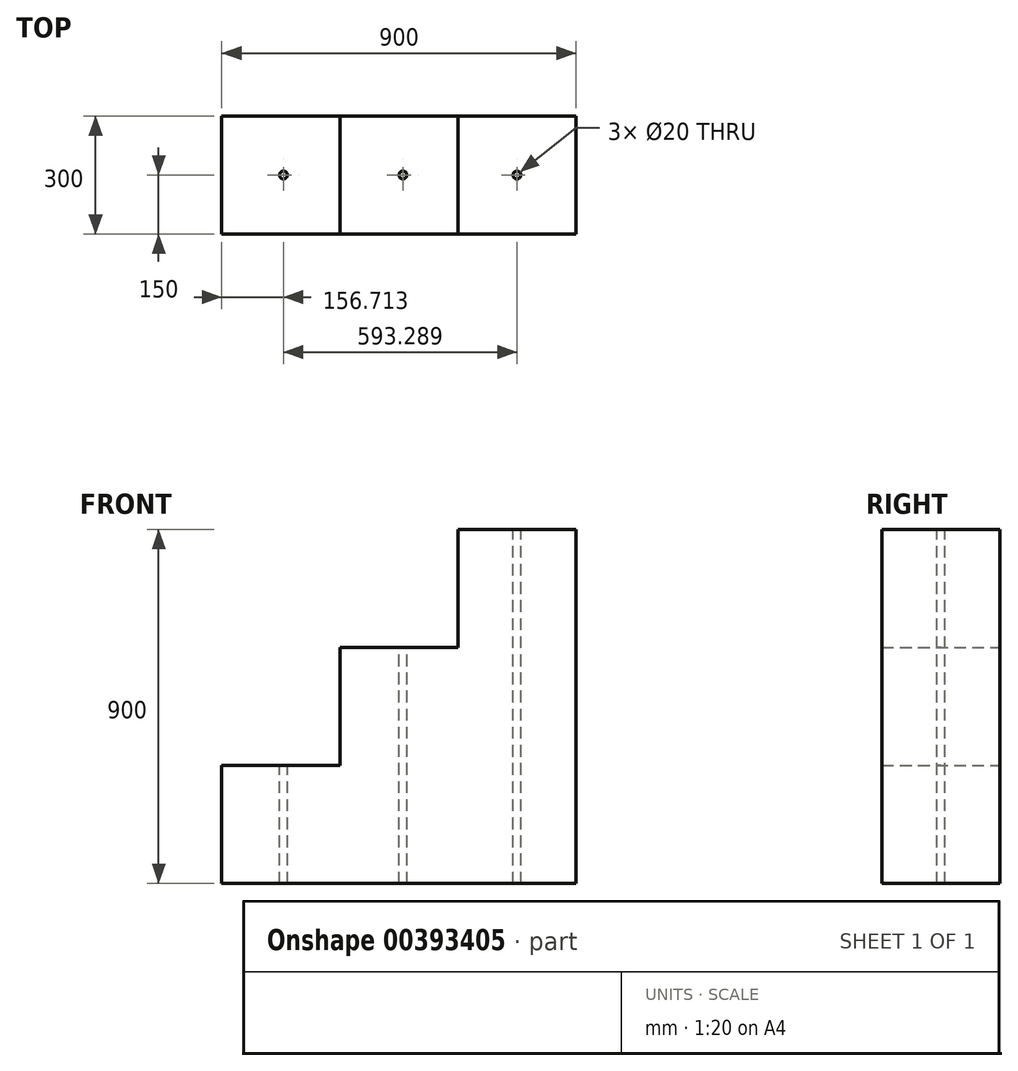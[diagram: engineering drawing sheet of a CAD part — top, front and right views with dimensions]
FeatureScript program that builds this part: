
annotation { "Feature Type Name" : "Feature", "Feature Type Description" : "" }
export const myFeature = defineFeature(function(context is Context, id is Id, definition is map)
    precondition{}
    {
        {
            var Q0;
            Q0=qCreatedBy(makeId("Front.planeOp"),FACE);
            var sketch = newSketch(context, id + "F0", { "sketchPlane" : qUnion([Q0])});
            skLineSegment(sketch, "E0", {"start": v(429.62, -452.95) * mm, "end": v(429.62, 447.05) * mm});
            skLineSegment(sketch, "E1", {"start": v(429.62, 447.05) * mm, "end": v(129.62, 447.05) * mm});
            skLineSegment(sketch, "E2", {"start": v(129.62, 447.05) * mm, "end": v(129.62, 147.05) * mm});
            skLineSegment(sketch, "E3", {"start": v(129.62, 147.05) * mm, "end": v(-170.38, 147.05) * mm});
            skLineSegment(sketch, "E4", {"start": v(-170.38, 147.05) * mm, "end": v(-170.38, -152.95) * mm});
            skLineSegment(sketch, "E5", {"start": v(-170.38, -152.95) * mm, "end": v(-470.38, -152.95) * mm});
            skLineSegment(sketch, "E6", {"start": v(-470.38, -152.95) * mm, "end": v(-470.38, -452.95) * mm});
            skLineSegment(sketch, "E7", {"start": v(-470.38, -452.95) * mm, "end": v(429.62, -452.95) * mm});
            skSolve(sketch);
        }
        {
            var Q0;
            Q0 = qSketchRegion(id + "F0", true);
            extrude(context, id + "F1", {"entities" : qUnion([Q0]), "depth" : 300 * mm});
        }
        {
            var Q0;
            Q0=makeQuery(id+"F1.opExtrude","SWEPT_FACE",FACE,{"disambiguationData":[OSD([sQuery(id+"F0.wireOp",EDGE,"E1")])]});
            var sketch = newSketch(context, id + "F2", { "sketchPlane" : qUnion([Q0])});
            skCircle(sketch, "E8", {"center": v(279.62, -150) * mm, "radius": 10 * mm});
            skPoint(sketch, "E8.centerSnap0", {"position": v(129.62, -150) * mm});
            skPoint(sketch, "E8.centerSnap1", {"position": v(279.62, 0) * mm});
            skCircle(sketch, "E9", {"center": v(-10.21, -150) * mm, "radius": 10 * mm});
            skCircle(sketch, "E10", {"center": v(-313.67, -150) * mm, "radius": 10 * mm});
            skSolve(sketch);
        }
        {
            var Q0;
            Q0 = qSketchRegion(id + "F2", true);
            extrude(context, id + "F3", {"entities" : qUnion([Q0]), "operationType" : NewBodyOperationType.REMOVE, "endBound" : BoundingType.THROUGH_ALL, "oppositeDirection" : true, "depth" : 25 * mm});
        }
    });
